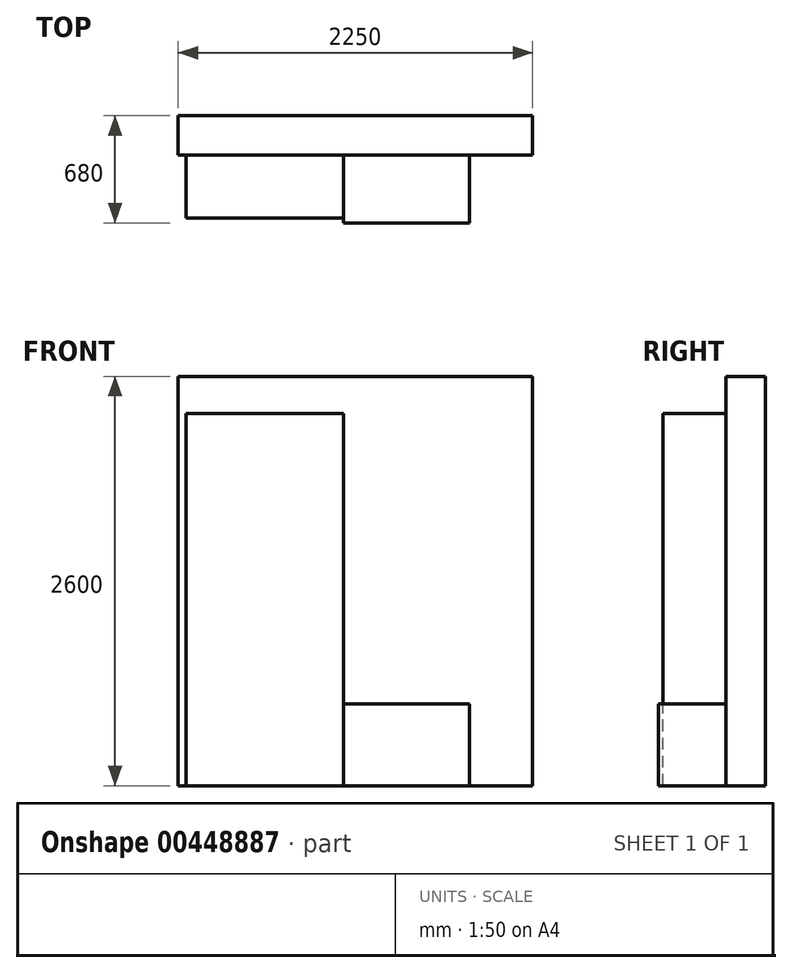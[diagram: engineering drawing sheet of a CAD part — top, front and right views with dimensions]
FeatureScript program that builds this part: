
annotation { "Feature Type Name" : "Feature", "Feature Type Description" : "" }
export const myFeature = defineFeature(function(context is Context, id is Id, definition is map)
    precondition{}
    {
        {
            var Q0;
            Q0=qCreatedBy(makeId("Front.planeOp"),FACE);
            var sketch = newSketch(context, id + "F0", { "sketchPlane" : qUnion([Q0])});
            skLineSegment(sketch, "E0.bottom", {"start": v(-50, 0) * mm, "end": v(2200, 0) * mm});
            skLineSegment(sketch, "E0.top", {"start": v(-50, 2600) * mm, "end": v(2200, 2600) * mm});
            skLineSegment(sketch, "E0.left", {"start": v(-50, 0) * mm, "end": v(-50, 2600) * mm});
            skLineSegment(sketch, "E0.right", {"start": v(2200, 0) * mm, "end": v(2200, 2600) * mm});
            skSolve(sketch);
        }
        {
            var Q0;
            Q0 = qSketchRegion(id + "F0", true);
            extrude(context, id + "F1", {"entities" : qUnion([Q0]), "oppositeDirection" : true, "depth" : 250 * mm});
        }
        {
            var Q0;
            Q0=qCreatedBy(makeId("Front.planeOp"),FACE);
            var sketch = newSketch(context, id + "F2", { "sketchPlane" : qUnion([Q0])});
            skLineSegment(sketch, "E1.bottom", {"start": v(0, 0) * mm, "end": v(1000, 0) * mm});
            skLineSegment(sketch, "E1.top", {"start": v(0, 2364) * mm, "end": v(1000, 2364) * mm});
            skLineSegment(sketch, "E1.left", {"start": v(0, 0) * mm, "end": v(0, 2364) * mm});
            skLineSegment(sketch, "E1.right", {"start": v(1000, 0) * mm, "end": v(1000, 2364) * mm});
            skSolve(sketch);
        }
        {
            var Q0;
            Q0 = qSketchRegion(id + "F2", true);
            extrude(context, id + "F3", {"entities" : qUnion([Q0]), "depth" : 400 * mm});
        }
        {
            var Q0;
            Q0=qCreatedBy(makeId("Front.planeOp"),FACE);
            var sketch = newSketch(context, id + "F4", { "sketchPlane" : qUnion([Q0])});
            skPoint(sketch, "E2.0", {"position": v(1000, 0) * mm});
            skLineSegment(sketch, "E3.bottom", {"start": v(1000, 0) * mm, "end": v(1800, 0) * mm});
            skLineSegment(sketch, "E3.top", {"start": v(1000, 520) * mm, "end": v(1800, 520) * mm});
            skLineSegment(sketch, "E3.left", {"start": v(1000, 0) * mm, "end": v(1000, 520) * mm});
            skLineSegment(sketch, "E3.right", {"start": v(1800, 0) * mm, "end": v(1800, 520) * mm});
            skSolve(sketch);
        }
        {
            var Q0;
            Q0 = qSketchRegion(id + "F4", true);
            extrude(context, id + "F5", {"entities" : qUnion([Q0]), "depth" : 430 * mm});
        }
    });
